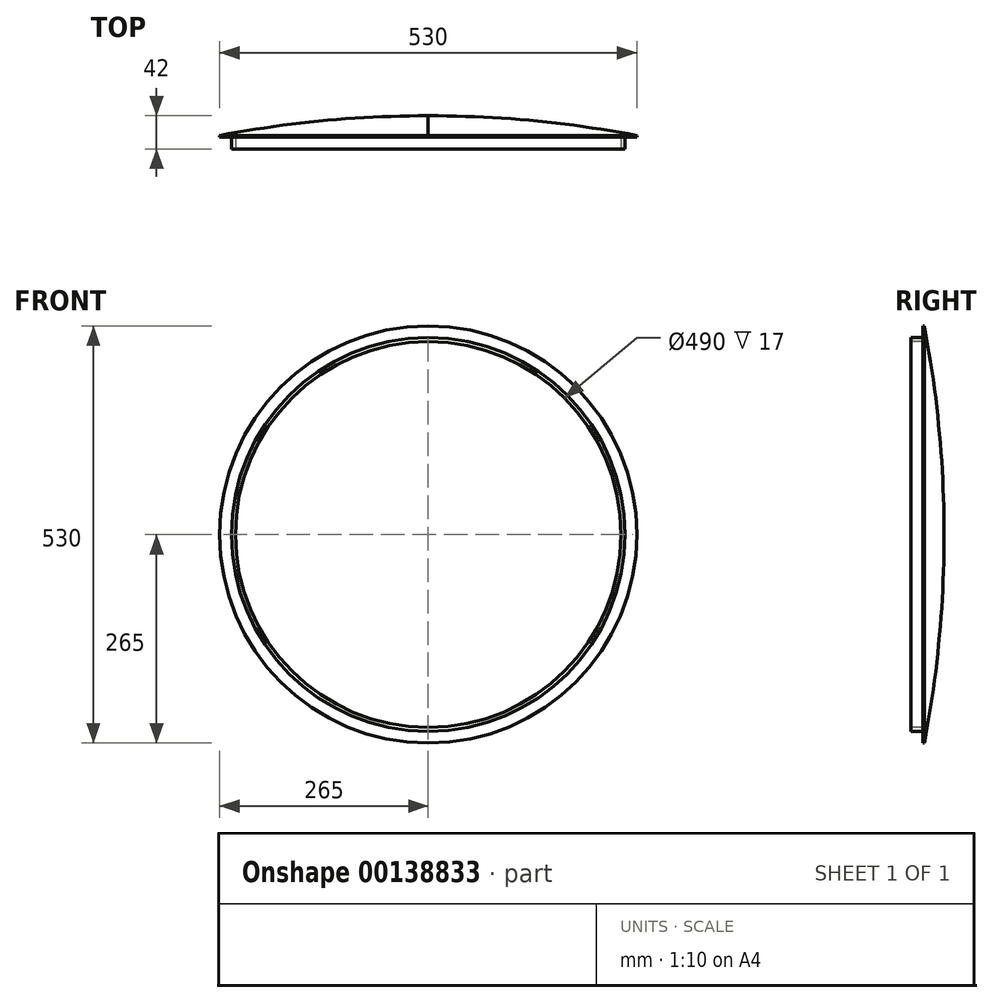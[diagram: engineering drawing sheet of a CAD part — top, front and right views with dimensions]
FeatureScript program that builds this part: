
annotation { "Feature Type Name" : "Feature", "Feature Type Description" : "" }
export const myFeature = defineFeature(function(context is Context, id is Id, definition is map)
    precondition{}
    {
        {
            var Q0;
            Q0=qCreatedBy(makeId("Top.planeOp"),FACE);
            var sketch = newSketch(context, id + "F0", { "sketchPlane" : qUnion([Q0])});
            skLineSegment(sketch, "E0", {"start": v(0, 0) * mm, "end": v(0, -200) * mm, "construction": true});
            skLineSegment(sketch, "E1", {"start": v(0, 0) * mm, "end": v(250, 0) * mm});
            skLineSegment(sketch, "E2", {"start": v(250, 0) * mm, "end": v(250, 15) * mm});
            skLineSegment(sketch, "E3", {"start": v(250, 15) * mm, "end": v(265, 15) * mm});
            skLineSegment(sketch, "E4", {"start": v(265, 15) * mm, "end": v(265, 17) * mm});
            skPoint(sketch, "E5.orphan", {"position": v(0, 200) * mm});
            skLineSegment(sketch, "E6", {"start": v(0, 0) * mm, "end": v(0, 42) * mm, "construction": true});
            skLineSegment(sketch, "E7", {"start": v(0, 42) * mm, "end": v(1, 42) * mm});
            skArc(sketch, "E8", {"start": v(265, 17) * mm, "mid": v(133.6, 35.74) * mm, "end": v(1, 42) * mm});
            skLineSegment(sketch, "E9", {"start": v(0, 42) * mm, "end": v(0, 0) * mm});
            skSolve(sketch);
        }
        {
            var Q0;
            Q0=makeQuery(id+"F0.imprint","IMPRINT",FACE,{"disambiguationData":[TD([[makeQuery(id+"F0.imprint","IMPRINT",EDGE,{"derivedFrom":sQuery(id+"F0.wireOp",EDGE,"E1")}),1.0]])]});
            var Q1;
            Q1=sQuery(id+"F0.wireOp",EDGE,"E9");
            revolve(context, id + "F1", {"entities" : qUnion([Q0]), "axis" : qUnion([Q1]), "revolveType" : RevolveType.FULL});
        }
        {
            var Q0;
            Q0=makeQuery(id+"F1.opRevolve","SWEPT_FACE",FACE,{"disambiguationData":[OSD([sQuery(id+"F0.wireOp",EDGE,"E1")])]});
            var sketch = newSketch(context, id + "F2", { "sketchPlane" : qUnion([Q0])});
            skCircle(sketch, "E10.0", {"center": v(0, 0) * mm, "radius": 245 * mm});
            skSolve(sketch);
        }
        {
            var Q0;
            Q0=makeQuery(id+"F2.imprint","IMPRINT",FACE,{"disambiguationData":[TD([[makeQuery(id+"F2.imprint","IMPRINT",EDGE,{"derivedFrom":sQuery(id+"F2.wireOp",EDGE,"E10.0")}),1.0]])]});
            extrude(context, id + "F3", {"entities" : qUnion([Q0]), "operationType" : NewBodyOperationType.REMOVE, "oppositeDirection" : true, "depth" : 17 * mm});
        }
    });
